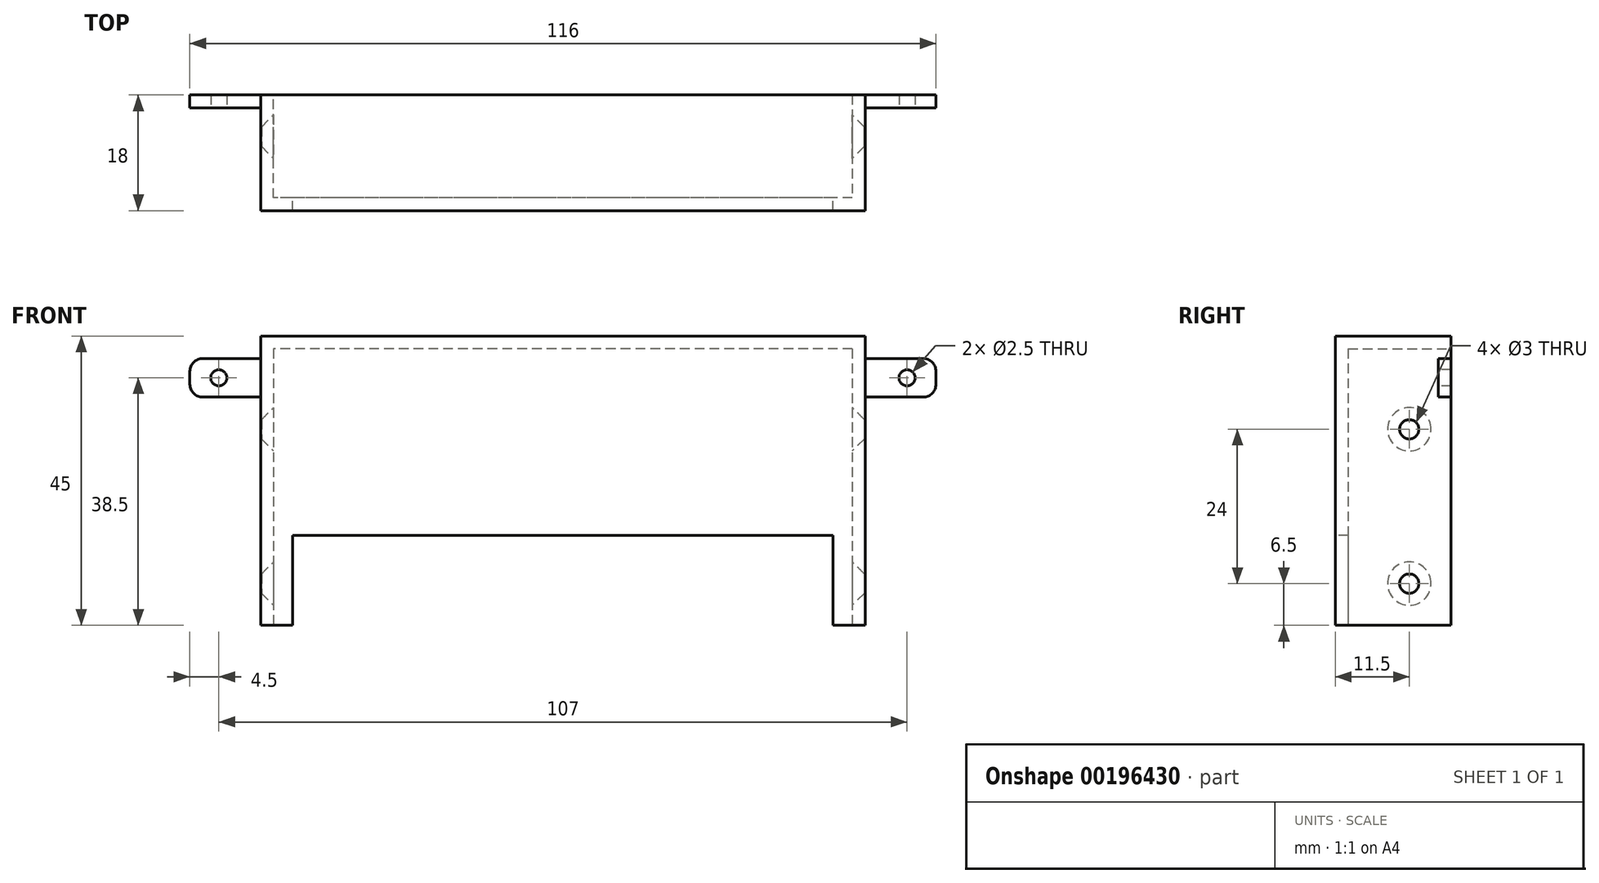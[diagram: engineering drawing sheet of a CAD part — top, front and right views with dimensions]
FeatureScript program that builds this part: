
annotation { "Feature Type Name" : "Feature", "Feature Type Description" : "" }
export const myFeature = defineFeature(function(context is Context, id is Id, definition is map)
    precondition{}
    {
        {
            var Q0;
            Q0=qCreatedBy(makeId("Front.planeOp"),FACE);
            var sketch = newSketch(context, id + "F0", { "sketchPlane" : qUnion([Q0])});
            skLineSegment(sketch, "E0.bottom", {"start": v(47, 22.5) * mm, "end": v(-47, 22.5) * mm});
            skLineSegment(sketch, "E0.top", {"start": v(47, -22.5) * mm, "end": v(-47, -22.5) * mm});
            skLineSegment(sketch, "E0.left", {"start": v(47, 22.5) * mm, "end": v(47, -22.5) * mm});
            skLineSegment(sketch, "E0.right", {"start": v(-47, 22.5) * mm, "end": v(-47, -22.5) * mm});
            skPoint(sketch, "E0.middle", {"position": v(0, 0) * mm});
            skSolve(sketch);
        }
        {
            var Q0;
            Q0=qSketchRegion(id+"F0",true);
            extrude(context, id + "F1", {"entities" : qUnion([Q0]), "depth" : 2 * mm});
        }
        {
            var Q0;
            Q0=makeQuery(id+"F1.opExtrude","CAP_FACE",FACE,{"disambiguationData":[OSD([sQuery(id+"F0.wireOp",EDGE,"E0.bottom"),sQuery(id+"F0.wireOp",EDGE,"E0.top"),sQuery(id+"F0.wireOp",EDGE,"E0.left"),sQuery(id+"F0.wireOp",EDGE,"E0.right")])],"isStart":true});
            var sketch = newSketch(context, id + "F2", { "sketchPlane" : qUnion([Q0])});
            skLineSegment(sketch, "E1.bottom", {"start": v(-47, 22.5) * mm, "end": v(-45, 22.5) * mm});
            skLineSegment(sketch, "E1.top", {"start": v(-47, -22.5) * mm, "end": v(-45, -22.5) * mm});
            skLineSegment(sketch, "E1.left", {"start": v(-47, 22.5) * mm, "end": v(-47, -22.5) * mm});
            skLineSegment(sketch, "E1.right", {"start": v(-45, 22.5) * mm, "end": v(-45, -22.5) * mm});
            skLineSegment(sketch, "E2.bottom", {"start": v(47, 22.5) * mm, "end": v(45, 22.5) * mm});
            skLineSegment(sketch, "E2.top", {"start": v(47, -22.5) * mm, "end": v(45, -22.5) * mm});
            skLineSegment(sketch, "E2.left", {"start": v(47, 22.5) * mm, "end": v(47, -22.5) * mm});
            skLineSegment(sketch, "E2.right", {"start": v(45, 22.5) * mm, "end": v(45, -22.5) * mm});
            skSolve(sketch);
        }
        {
            var Q0;
            Q0=qSketchRegion(id+"F2",true);
            extrude(context, id + "F3", {"entities" : qUnion([Q0]), "operationType" : NewBodyOperationType.ADD, "depth" : 16 * mm});
        }
        {
            var Q0;
            Q0=makeQuery(id+"F3.boolean.opBoolean","MERGE",FACE,{"derivedFrom":[makeQuery(id+"F1.opExtrude","SWEPT_FACE",FACE,{"disambiguationData":[OSD([sQuery(id+"F0.wireOp",EDGE,"E0.bottom")])]}),makeQuery(id+"F3.opExtrude","SWEPT_FACE",FACE,{"disambiguationData":[OSD([sQuery(id+"F2.wireOp",EDGE,"E1.bottom")])]}),makeQuery(id+"F3.opExtrude","SWEPT_FACE",FACE,{"disambiguationData":[OSD([sQuery(id+"F2.wireOp",EDGE,"E2.bottom")])]})]});
            var sketch = newSketch(context, id + "F4", { "sketchPlane" : qUnion([Q0])});
            skLineSegment(sketch, "E3.bottom", {"start": v(-47, -2) * mm, "end": v(47, -2) * mm});
            skLineSegment(sketch, "E3.top", {"start": v(-47, 16) * mm, "end": v(47, 16) * mm});
            skLineSegment(sketch, "E3.left", {"start": v(-47, -2) * mm, "end": v(-47, 16) * mm});
            skLineSegment(sketch, "E3.right", {"start": v(47, -2) * mm, "end": v(47, 16) * mm});
            skSolve(sketch);
        }
        {
            var Q0;
            Q0=qSketchRegion(id+"F4",true);
            extrude(context, id + "F5", {"entities" : qUnion([Q0]), "operationType" : NewBodyOperationType.ADD, "oppositeDirection" : true, "depth" : 2 * mm});
        }
        {
            var Q0;
            Q0=makeQuery(id+"F3.boolean.opBoolean","MERGE",FACE,{"derivedFrom":[makeQuery(id+"F1.opExtrude","SWEPT_FACE",FACE,{"disambiguationData":[OSD([sQuery(id+"F0.wireOp",EDGE,"E0.left")])]}),makeQuery(id+"F3.opExtrude","SWEPT_FACE",FACE,{"disambiguationData":[OSD([sQuery(id+"F2.wireOp",EDGE,"E1.left")])]})]});
            var sketch = newSketch(context, id + "F6", { "sketchPlane" : qUnion([Q0])});
            skLineSegment(sketch, "E4", {"start": v(16, 22.5) * mm, "end": v(16, -22.5) * mm, "construction": true});
            skLineSegment(sketch, "E5", {"start": v(16, -22.5) * mm, "end": v(-2, -22.5) * mm, "construction": true});
            skLineSegment(sketch, "E6", {"start": v(-2, -22.5) * mm, "end": v(-2, 0) * mm, "construction": true});
            skLineSegment(sketch, "E7", {"start": v(-2, 0) * mm, "end": v(44.18, 0) * mm, "construction": true});
            skLineSegment(sketch, "E8.bottom", {"start": v(16, 19) * mm, "end": v(14, 19) * mm});
            skLineSegment(sketch, "E8.top", {"start": v(16, 13) * mm, "end": v(14, 13) * mm});
            skLineSegment(sketch, "E8.left", {"start": v(16, 19) * mm, "end": v(16, 13) * mm});
            skLineSegment(sketch, "E8.right", {"start": v(14, 19) * mm, "end": v(14, 13) * mm});
            skLineSegment(sketch, "E9.bottom", {"start": v(16, -13) * mm, "end": v(14, -13) * mm});
            skLineSegment(sketch, "E9.top", {"start": v(16, -19) * mm, "end": v(14, -19) * mm});
            skLineSegment(sketch, "E9.left", {"start": v(16, -13) * mm, "end": v(16, -19) * mm});
            skLineSegment(sketch, "E9.right", {"start": v(14, -13) * mm, "end": v(14, -19) * mm});
            skSolve(sketch);
        }
        {
            var Q0;
            Q0=qSketchRegion(id+"F6",true);
            extrude(context, id + "F7", {"entities" : qUnion([Q0]), "operationType" : NewBodyOperationType.ADD, "depth" : 11 * mm});
        }
        {
            var Q0;
            Q0=makeQuery(id+"F7.opExtrude","SWEPT_FACE",FACE,{"disambiguationData":[OSD([sQuery(id+"F6.wireOp",EDGE,"E8.right")])]});
            var sketch = newSketch(context, id + "F8", { "sketchPlane" : qUnion([Q0])});
            skCircle(sketch, "E10", {"center": v(53.5, 16) * mm, "radius": 1.25 * mm});
            skCircle(sketch, "E11", {"center": v(53.5, -16) * mm, "radius": 1.5 * mm});
            skSolve(sketch);
        }
        {
            var Q0;
            Q0=qSketchRegion(id+"F8",true);
            extrude(context, id + "F9", {"entities" : qUnion([Q0]), "operationType" : NewBodyOperationType.REMOVE, "oppositeDirection" : true, "depth" : 25 * mm});
        }
        {
            var Q0;
            Q0=makeQuery(id+"F7.opExtrude","CAP_EDGE",EDGE,{"disambiguationData":[OSD([sQuery(id+"F6.wireOp",EDGE,"E9.top")])],"isStart":false});
            var Q1;
            Q1=makeQuery(id+"F7.opExtrude","CAP_EDGE",EDGE,{"disambiguationData":[OSD([sQuery(id+"F6.wireOp",EDGE,"E9.bottom")])],"isStart":false});
            var Q2;
            Q2=makeQuery(id+"F7.opExtrude","CAP_EDGE",EDGE,{"disambiguationData":[OSD([sQuery(id+"F6.wireOp",EDGE,"E8.bottom")])],"isStart":false});
            var Q3;
            Q3=makeQuery(id+"F7.opExtrude","CAP_EDGE",EDGE,{"disambiguationData":[OSD([sQuery(id+"F6.wireOp",EDGE,"E8.top")])],"isStart":false});
            var Q4;
            Q4=makeQuery(id+"F7.opExtrude","CAP_EDGE",EDGE,{"disambiguationData":[OSD([sQuery(id+"F6.wireOp",EDGE,"E9.right")])],"isStart":true});
            var Q5;
            Q5=makeQuery(id+"F7.opExtrude","CAP_EDGE",EDGE,{"disambiguationData":[OSD([sQuery(id+"F6.wireOp",EDGE,"E8.right")])],"isStart":true});
            fillet(context, id + "F10", {"entities" : qUnion([Q0, Q1, Q2, Q3, Q4, Q5]), "radius" : 2 * mm, "tangentPropagation" : true, "allowEdgeOverflow" : false});
        }
        {
            var Q0;
            Q0=makeQuery(id+"F1.opExtrude","SWEPT_BODY",BODY,{"disambiguationData":[OSD([sQuery(id+"F0.wireOp",EDGE,"E0.bottom"),sQuery(id+"F0.wireOp",EDGE,"E0.top"),sQuery(id+"F0.wireOp",EDGE,"E0.left"),sQuery(id+"F0.wireOp",EDGE,"E0.right")])]});
            var Q1;
            Q1=qCreatedBy(makeId("Right.planeOp"),FACE);
            mirror(context, id + "F11", {"operationType" : NewBodyOperationType.ADD, "entities" : qUnion([Q0]), "mirrorPlane" : qUnion([Q1])});
        }
        {
            var Q0;
            Q0=makeQuery(id+"F1.opExtrude","CAP_FACE",FACE,{"disambiguationData":[OSD([sQuery(id+"F0.wireOp",EDGE,"E0.bottom"),sQuery(id+"F0.wireOp",EDGE,"E0.top"),sQuery(id+"F0.wireOp",EDGE,"E0.left"),sQuery(id+"F0.wireOp",EDGE,"E0.right")])],"isStart":false});
            var sketch = newSketch(context, id + "F12", { "sketchPlane" : qUnion([Q0])});
            skLineSegment(sketch, "E12.bottom", {"start": v(47, -22.5) * mm, "end": v(66.27, -22.5) * mm});
            skLineSegment(sketch, "E12.top", {"start": v(47, -7.64) * mm, "end": v(66.27, -7.64) * mm});
            skLineSegment(sketch, "E12.left", {"start": v(47, -22.5) * mm, "end": v(47, -7.64) * mm});
            skLineSegment(sketch, "E12.right", {"start": v(66.27, -22.5) * mm, "end": v(66.27, -7.64) * mm});
            skLineSegment(sketch, "E13.bottom", {"start": v(-47, -22.5) * mm, "end": v(-63.88, -22.5) * mm});
            skLineSegment(sketch, "E13.top", {"start": v(-47, -7.22) * mm, "end": v(-63.88, -7.22) * mm});
            skLineSegment(sketch, "E13.left", {"start": v(-47, -22.5) * mm, "end": v(-47, -7.22) * mm});
            skLineSegment(sketch, "E13.right", {"start": v(-63.88, -22.5) * mm, "end": v(-63.88, -7.22) * mm});
            skSolve(sketch);
        }
        {
            var Q0;
            Q0=qSketchRegion(id+"F12",true);
            extrude(context, id + "F13", {"entities" : qUnion([Q0]), "operationType" : NewBodyOperationType.REMOVE, "oppositeDirection" : true, "depth" : 25 * mm});
        }
        {
            var Q0;
            Q0=makeQuery(id+"F13.boolean.opBoolean","MERGE",FACE,{"derivedFrom":[makeQuery(id+"F3.boolean.opBoolean","MERGE",FACE,{"derivedFrom":[makeQuery(id+"F1.opExtrude","SWEPT_FACE",FACE,{"disambiguationData":[OSD([sQuery(id+"F0.wireOp",EDGE,"E0.right")])]}),makeQuery(id+"F3.opExtrude","SWEPT_FACE",FACE,{"disambiguationData":[OSD([sQuery(id+"F2.wireOp",EDGE,"E2.left")])]})]}),makeQuery(id+"F13.opExtrude","SWEPT_FACE",FACE,{"disambiguationData":[OSD([sQuery(id+"F12.wireOp",EDGE,"E13.left")])]})]});
            var sketch = newSketch(context, id + "F14", { "sketchPlane" : qUnion([Q0])});
            skCircle(sketch, "E14", {"center": v(-9.5, -16) * mm, "radius": 1.5 * mm});
            skSolve(sketch);
        }
        {
            var Q0;
            Q0=qSketchRegion(id+"F14",true);
            extrude(context, id + "F15", {"entities" : qUnion([Q0]), "operationType" : NewBodyOperationType.REMOVE, "oppositeDirection" : true, "depth" : 100 * mm});
        }
        {
            var Q0;
            Q0=makeQuery(id+"F13.boolean.opBoolean","MERGE",FACE,{"derivedFrom":[makeQuery(id+"F3.boolean.opBoolean","MERGE",FACE,{"derivedFrom":[makeQuery(id+"F1.opExtrude","SWEPT_FACE",FACE,{"disambiguationData":[OSD([sQuery(id+"F0.wireOp",EDGE,"E0.right")])]}),makeQuery(id+"F3.opExtrude","SWEPT_FACE",FACE,{"disambiguationData":[OSD([sQuery(id+"F2.wireOp",EDGE,"E2.left")])]})]}),makeQuery(id+"F13.opExtrude","SWEPT_FACE",FACE,{"disambiguationData":[OSD([sQuery(id+"F12.wireOp",EDGE,"E13.left")])]})]});
            var sketch = newSketch(context, id + "F16", { "sketchPlane" : qUnion([Q0])});
            skCircle(sketch, "E15", {"center": v(-9.5, 8) * mm, "radius": 1.5 * mm});
            skSolve(sketch);
        }
        {
            var Q0;
            Q0=qSketchRegion(id+"F16",true);
            extrude(context, id + "F17", {"entities" : qUnion([Q0]), "operationType" : NewBodyOperationType.REMOVE, "oppositeDirection" : true, "depth" : 100 * mm});
        }
        {
            var Q0;
            Q0=makeQuery(id+"F17.boolean.opBoolean","INTERSECT",EDGE,{"derivedFrom":[makeQuery(id+"F3.opExtrude","SWEPT_FACE",FACE,{"disambiguationData":[OSD([sQuery(id+"F2.wireOp",EDGE,"E1.right")])]}),makeQuery(id+"F17.opExtrude","SWEPT_FACE",FACE,{"disambiguationData":[OSD([sQuery(id+"F16.wireOp",EDGE,"E15")])]})]});
            var Q1;
            Q1=makeQuery(id+"F15.boolean.opBoolean","INTERSECT",EDGE,{"derivedFrom":[makeQuery(id+"F3.opExtrude","SWEPT_FACE",FACE,{"disambiguationData":[OSD([sQuery(id+"F2.wireOp",EDGE,"E1.right")])]}),makeQuery(id+"F15.opExtrude","SWEPT_FACE",FACE,{"disambiguationData":[OSD([sQuery(id+"F14.wireOp",EDGE,"E14")])]})]});
            var Q2;
            Q2=makeQuery(id+"F17.boolean.opBoolean","INTERSECT",EDGE,{"derivedFrom":[makeQuery(id+"F3.opExtrude","SWEPT_FACE",FACE,{"disambiguationData":[OSD([sQuery(id+"F2.wireOp",EDGE,"E2.right")])]}),makeQuery(id+"F17.opExtrude","SWEPT_FACE",FACE,{"disambiguationData":[OSD([sQuery(id+"F16.wireOp",EDGE,"E15")])]})]});
            var Q3;
            Q3=makeQuery(id+"F15.boolean.opBoolean","INTERSECT",EDGE,{"derivedFrom":[makeQuery(id+"F3.opExtrude","SWEPT_FACE",FACE,{"disambiguationData":[OSD([sQuery(id+"F2.wireOp",EDGE,"E2.right")])]}),makeQuery(id+"F15.opExtrude","SWEPT_FACE",FACE,{"disambiguationData":[OSD([sQuery(id+"F14.wireOp",EDGE,"E14")])]})]});
            chamfer(context, id + "F18", {"entities" : qUnion([Q0, Q1, Q2, Q3]), "width" : 1.87 * mm, "tangentPropagation" : true});
        }
        {
            var Q0;
            Q0=makeQuery(id+"F1.opExtrude","CAP_FACE",FACE,{"disambiguationData":[OSD([sQuery(id+"F0.wireOp",EDGE,"E0.bottom"),sQuery(id+"F0.wireOp",EDGE,"E0.top"),sQuery(id+"F0.wireOp",EDGE,"E0.left"),sQuery(id+"F0.wireOp",EDGE,"E0.right")])],"isStart":false});
            var sketch = newSketch(context, id + "F19", { "sketchPlane" : qUnion([Q0])});
            skLineSegment(sketch, "E16.bottom", {"start": v(42, -8.5) * mm, "end": v(-42, -8.5) * mm});
            skLineSegment(sketch, "E16.top", {"start": v(42, -36.5) * mm, "end": v(-42, -36.5) * mm});
            skLineSegment(sketch, "E16.left", {"start": v(42, -8.5) * mm, "end": v(42, -36.5) * mm});
            skLineSegment(sketch, "E16.right", {"start": v(-42, -8.5) * mm, "end": v(-42, -36.5) * mm});
            skPoint(sketch, "E16.middle", {"position": v(0, -22.5) * mm});
            skSolve(sketch);
        }
        {
            var Q0;
            Q0 = qSketchRegion(id + "F19", true);
            extrude(context, id + "F20", {"entities" : qUnion([Q0]), "operationType" : NewBodyOperationType.REMOVE, "oppositeDirection" : true, "depth" : 25 * mm});
        }
    });
